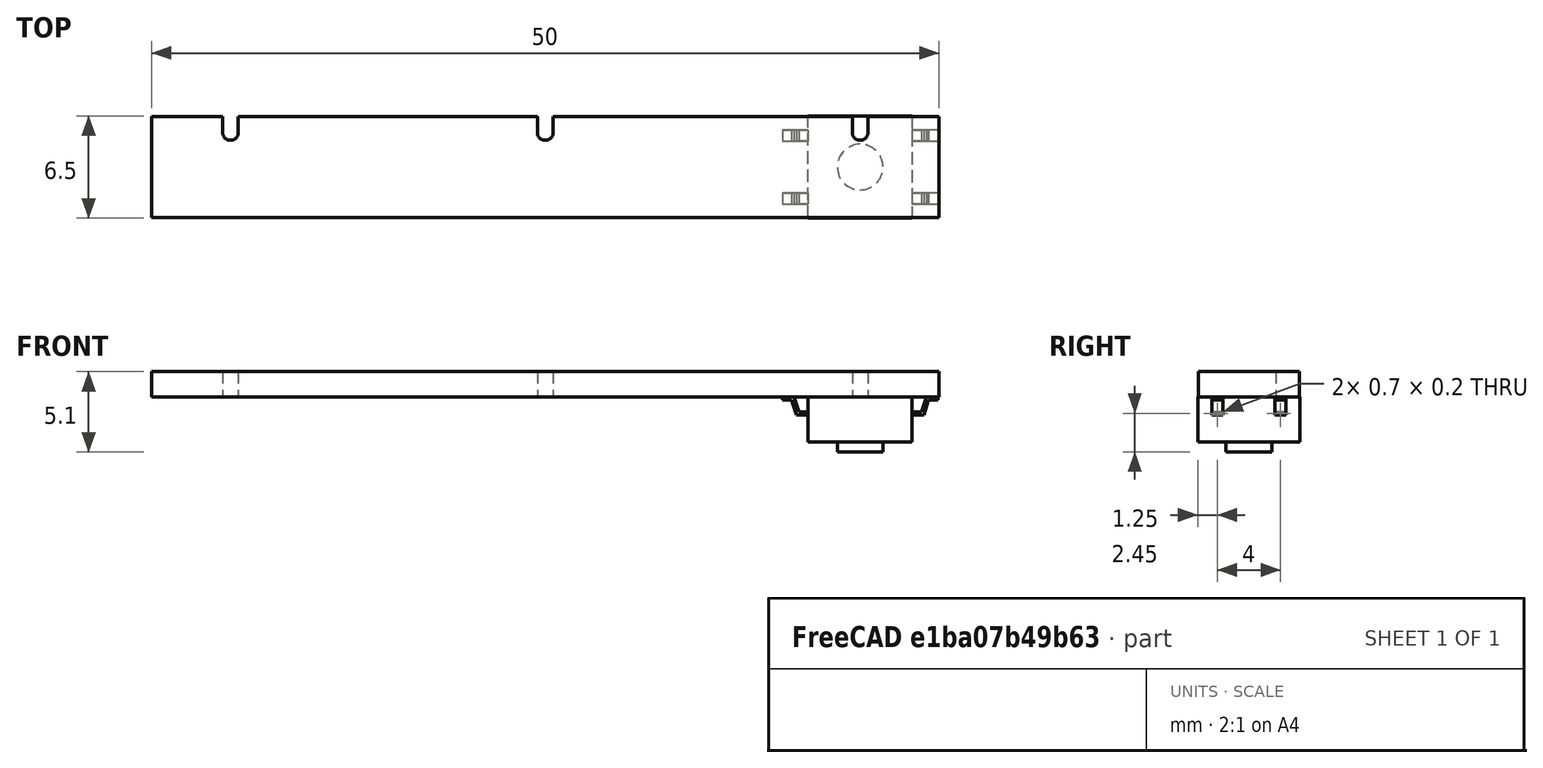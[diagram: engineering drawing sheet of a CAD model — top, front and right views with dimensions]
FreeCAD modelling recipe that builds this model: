
FCSTD DOCUMENT  (FreeCAD 2022.430R28641 (Git))
Label: futaba_base_v0r2-OnlyButtom
License: All rights reserved
LicenseURL: http://en.wikipedia.org/wiki/All_rights_reserved
objects: App::Part×4, App::Link×4, Part::Feature×2
note: 2 computed .brp shape members not serialized (recipe doc carries the construction recipe); baked Part::Feature solids carry a one-line shape summary decoded from their .brp

FEATURE [Part::Feature] Pcb_8054
  TreeRank = 0
  shape: bbox 50 x 6.4 x 1.6 mm, 21 faces (baked)
FEATURE [App::Part] Board_Geoms_8054
  ClaimAllChildren = false
  ExportMode = 1
  Group = -> [Pcb_8054]
  Origin = -> Origin
  TreeRank = 0
  _ExportChildren = -> [Pcb_8054]
  _GroupVersion = 1
FEATURE [Part::Feature] Shape  label="SW5_Áã¼þ1_ff458c263895"
  Placement = pos=(45,3.2,-1.6) rot=(0,0.707107,-0.707107;3.14159rad)
  TreeRank = 0
  shape: bbox 9.9 x 6.5 x 3.5 mm, 45 faces (baked)
FEATURE [App::Link] SW5_________1_ff458c263895_ln_  label="SW3_Áã¼þ1_bfd08f6032b9"
  AutoLinkLabel = false
  AutoPlacement = true
  LinkPlacement = pos=(25,3.2,-1.6) rot=(0,0.707107,-0.707107;3.14159rad)
  LinkedObject = -> Shape
  Placement = pos=(25,3.2,-1.6) rot=(0,0.707107,-0.707107;3.14159rad)
  SyncGroupVisibility = false
  TreeRank = 0
  _LinkVersion = 1
FEATURE [App::Link] SW5_________1_ff458c263895_ln_001  label="SW1_Áã¼þ1_d8c861bfb7ac"
  AutoLinkLabel = false
  AutoPlacement = true
  LinkPlacement = pos=(5,3.2,-1.6) rot=(0,0.707107,-0.707107;3.14159rad)
  LinkedObject = -> Shape
  Placement = pos=(5,3.2,-1.6) rot=(0,0.707107,-0.707107;3.14159rad)
  SyncGroupVisibility = false
  TreeRank = 0
  _LinkVersion = 1
FEATURE [App::Link] SW5_________1_ff458c263895_ln_002  label="SW2_Áã¼þ1_0276e8dd2714"
  AutoLinkLabel = false
  AutoPlacement = true
  LinkPlacement = pos=(15,3.2,-1.6) rot=(0,0.707107,-0.707107;3.14159rad)
  LinkedObject = -> Shape
  Placement = pos=(15,3.2,-1.6) rot=(0,0.707107,-0.707107;3.14159rad)
  SyncGroupVisibility = false
  TreeRank = 0
  _LinkVersion = 1
FEATURE [App::Link] SW5_________1_ff458c263895_ln_003  label="SW4_Áã¼þ1_75ba99306a9d"
  AutoLinkLabel = false
  AutoPlacement = true
  LinkPlacement = pos=(35,3.2,-1.6) rot=(0,0.707107,-0.707107;3.14159rad)
  LinkedObject = -> Shape
  Placement = pos=(35,3.2,-1.6) rot=(0,0.707107,-0.707107;3.14159rad)
  SyncGroupVisibility = false
  TreeRank = 0
  _LinkVersion = 1
FEATURE [App::Part] Bot_8054
  ClaimAllChildren = false
  ExportMode = 1
  Group = -> [Shape,SW5_________1_ff458c263895_ln_,SW5_________1_ff458c263895_ln_001,SW5_________1_ff458c263895_ln_002,SW5_________1_ff458c263895_ln_003]
  Origin = -> Origin004
  TreeRank = 0
  _ExportChildren = -> [Shape,SW5_________1_ff458c263895_ln_,SW5_________1_ff458c263895_ln_001,SW5_________1_ff458c263895_ln_002,SW5_________1_ff458c263895_ln_003]
  _GroupVersion = 1
FEATURE [App::Part] Step_Models_8054
  ClaimAllChildren = false
  ExportMode = 1
  Group = -> [Bot_8054]
  Origin = -> Origin002
  TreeRank = 0
  _ExportChildren = -> [Bot_8054]
  _GroupVersion = 1
FEATURE [App::Part] Board_8054  label="futaba_base_v0r2-OnlyButtom"
  ClaimAllChildren = false
  ExportMode = 1
  Group = -> [Board_Geoms_8054,Step_Models_8054]
  Origin = -> Origin001
  TreeRank = 0
  _ExportChildren = -> [Board_Geoms_8054,Step_Models_8054]
  _GroupVersion = 1
